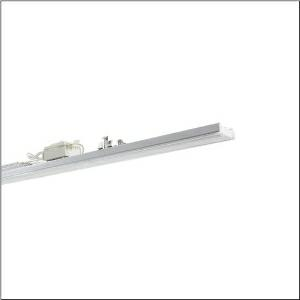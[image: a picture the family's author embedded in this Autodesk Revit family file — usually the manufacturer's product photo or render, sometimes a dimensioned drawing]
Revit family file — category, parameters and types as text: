
# Revit family: licross_21_recessed_ho_52tl12dv4lxm3s4
name_source: partatom
category: Lighting Fixtures
units: mm (PartAtom-declared; Revit-internal decimal feet)

## family parameters
Cut with Voids When Loaded = No
Host = Face
Light Source = No
Part Type = Normal
Room Calculation Point = No
Round Connector Dimension = Use Diameter
Shared = No

## types (1)
- --- (1 x LED, 20000 lm, 113.5 W, 4000K)
    Apparent Load = 114 VA
    CIE Flux Codes = 69 91 98 100 100
    Color Rendering = 80
    Color Temperature = 4000K
    Default Elevation = 1800 mm
    Description = Licross 21 Recessed HO, luminaire insert, of sheet steel, galvanised, coil coated, white, length: 2.250mm, width: 66mm, height: 67mm, LED rated luminous flux: 20.000lm, light colour: 840, SDCM (Standard Deviation of Colour Matching)MacAdam ≤ 3 SDCM (initial), control gear: DALI 2, with plug, 6-pole, with phase selection, for trunking rail, 9 or 11-core, mains connection: 220..240V, AC, 50/60Hz, rated input power: 114W, for emergency light function, internal wiring halogen-free, for trunking rail, 9-/11-core, converter,control gear: single battery element, battery: LiFePO4, 9Ah, primary optical cover: cover, of PMMA, light emission: direct distribution, primary light characteristic: symmetric, protection rating (complete): IP40, insulation class (complete): insulation class I (protective earthing), certification: CE, UKCA, protection symbol: D if used in an environment without relevant dust loads with corresponding accessories, impact resistance: IK06, permissible ambient temperature for indoor applications: +5..+35°C, standard: EN 60598-2-22, corresponds to IFS (International Featured Standards) requirements for safety and quality in the food industry, reducing of maximum allowable ambient temperature of 5°C with ceiling mounting, LABS conformity tested according to VDMA 24364:2018-05, The light source and the operating device comply with the requirements of the Ecodesign Regulation (EU) 2019/2020 and are replaceable in accordance with this regulation, packaging unit: 1 piece
    Height = 58 mm
    Lamp = 1 x LED
    Lamp Light Flux = 20000 lm
    Lamp Power = 113.5 W
    Lamp count = 1
    Length = 2250 mm
    Luminous efficacy = 176 lm/W
    Manufacturer = Siteco
    ModVariant = No
    Model = 52TL12DV4LXM3S4
    Mounting Place = Ceiling
    Mounting Type = Pendant
    Number of Poles = 1
    OnlyDefault = Yes
    Power Factor = 1
    Product Name = Licross 21 Recessed HO
    Product group = luminaire insert | ceiling pendant
    ProductGroupID = 901
    Protection Class = Protection class I
    Protection Degree = IP 40
    RLX_Detail_Level = 1
    RLX_Emergency_Light_Flux = 0 lm
    RLX_Emergency_Type = 0
    RLX_Emergency_Type_DB = No
    RlxData = <blob elided: 30185 chars, md5=1649d1e3>
    Socket = socket
    Standby Power = 0 W
    System Light Flux = 20000 lm
    System Power = 114 W
    Type Comments = : AC-mode, luminous flux: 100 % | dim-lin: 254 | 425 mA
    Type Image = l_1296930.jpg
    URL = http://relux.com
    VarID = @adj_036959
    Voltage = 0 V
    Weight = 0.00 kg
    Width = 66 mm

## geometry (parser evidence)
native form markers: Blend x4, Sweep x10
no freeform markers — native parametric forms only
